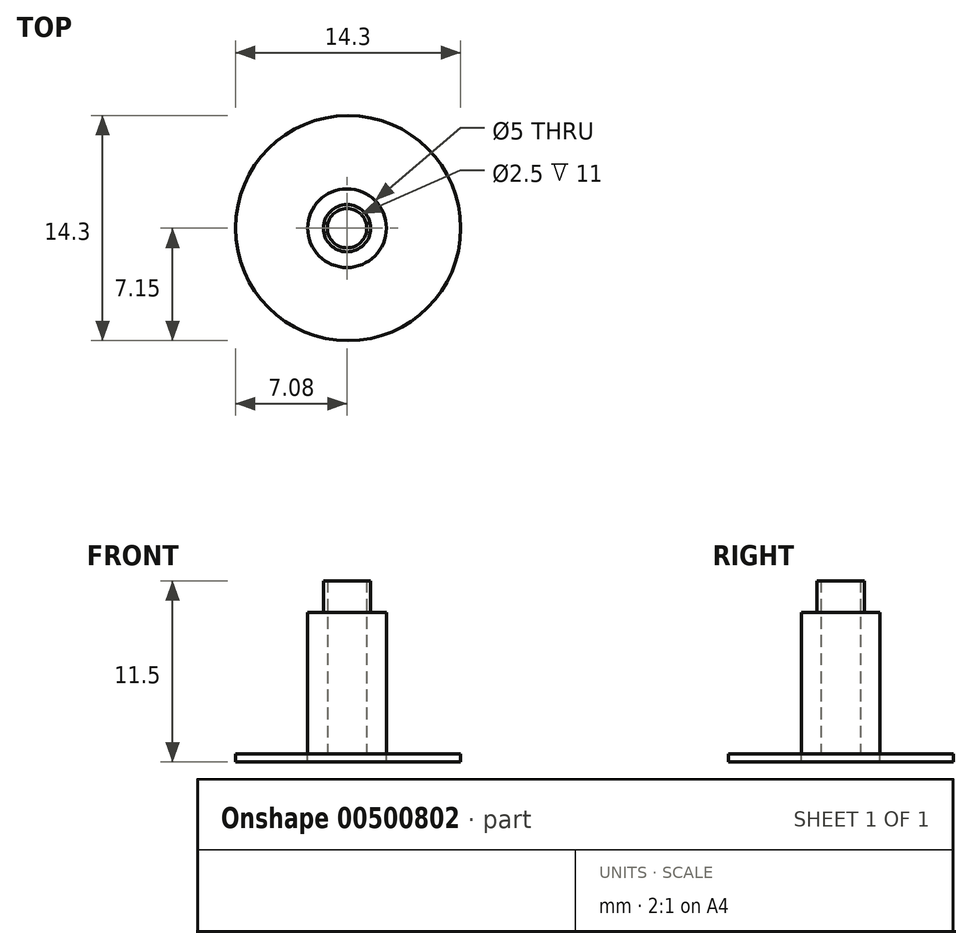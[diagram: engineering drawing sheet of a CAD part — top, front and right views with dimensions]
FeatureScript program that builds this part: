
annotation { "Feature Type Name" : "Feature", "Feature Type Description" : "" }
export const myFeature = defineFeature(function(context is Context, id is Id, definition is map)
    precondition{}
    {
        {
            var Q0;
            Q0=qCreatedBy(makeId("Top.planeOp"),FACE);
            var sketch = newSketch(context, id + "F0", { "sketchPlane" : qUnion([Q0])});
            skCircle(sketch, "E0", {"center": v(0, 0) * mm, "radius": 2.5 * mm});
            skCircle(sketch, "E1", {"center": v(0, 0) * mm, "radius": 1.5 * mm});
            skCircle(sketch, "E2", {"center": v(0, 0) * mm, "radius": 1.25 * mm});
            skCircle(sketch, "E3", {"center": v(0.07, 0) * mm, "radius": 7.15 * mm});
            skSolve(sketch);
        }
        {
            var Q0;
            Q0=makeQuery(id+"F0.imprint","IMPRINT",FACE,{"disambiguationData":[TD([[makeQuery(id+"F0.imprint","IMPRINT",EDGE,{"derivedFrom":sQuery(id+"F0.wireOp",EDGE,"E0")}),1.0]])]});
            extrude(context, id + "F1", {"entities" : qUnion([Q0]), "depth" : 9 * mm, "offsetDistance" : 25 * mm});
        }
        {
            var Q0;
            Q0=makeQuery(id+"F0.imprint","IMPRINT",FACE,{"disambiguationData":[TD([[makeQuery(id+"F0.imprint","IMPRINT",EDGE,{"derivedFrom":sQuery(id+"F0.wireOp",EDGE,"E1")}),1.0]])]});
            extrude(context, id + "F2", {"entities" : qUnion([Q0]), "operationType" : NewBodyOperationType.ADD, "depth" : 11 * mm, "offsetDistance" : 25 * mm});
        }
        {
            var Q0;
            Q0=makeQuery(id+"F0.imprint","IMPRINT",FACE,{"disambiguationData":[TD([[makeQuery(id+"F0.imprint","IMPRINT",EDGE,{"derivedFrom":sQuery(id+"F0.wireOp",EDGE,"E0")}),-1.0]])]});
            extrude(context, id + "F3", {"entities" : qUnion([Q0]), "oppositeDirection" : true, "depth" : .5 * mm, "offsetDistance" : 25 * mm});
        }
    });
